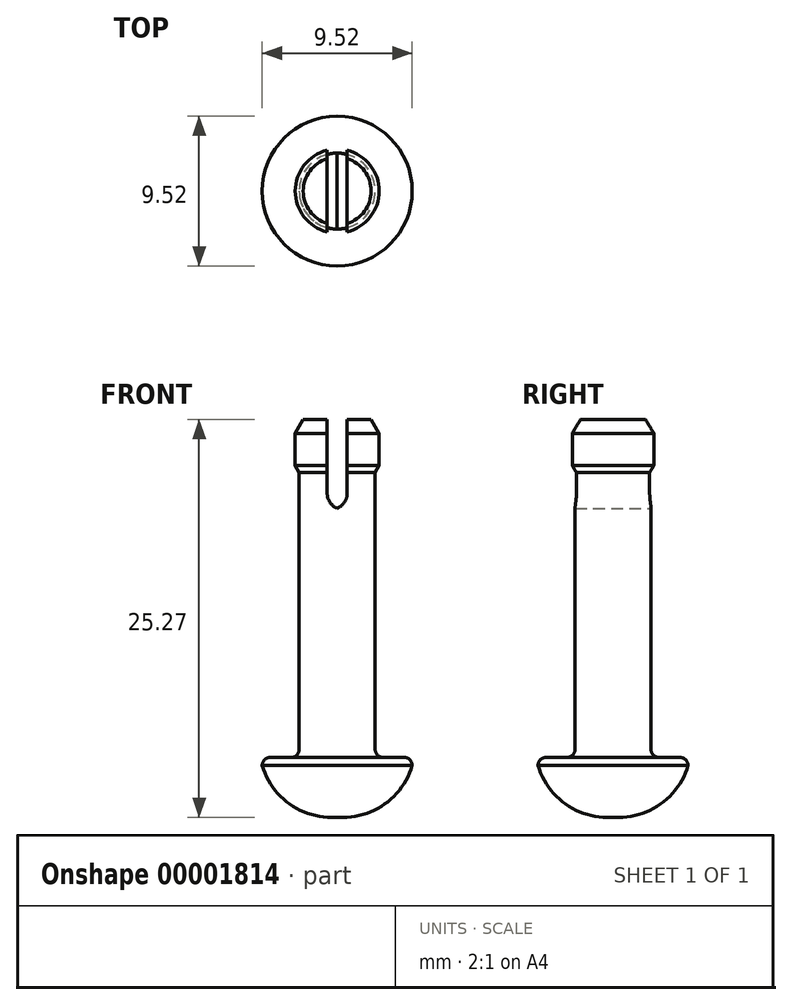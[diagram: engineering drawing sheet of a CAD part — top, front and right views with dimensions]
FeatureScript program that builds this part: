
annotation { "Feature Type Name" : "Feature", "Feature Type Description" : "" }
export const myFeature = defineFeature(function(context is Context, id is Id, definition is map)
    precondition{}
    {
        {
            var Q0;
            Q0=qCreatedBy(makeId("Front.planeOp"),FACE);
            var sketch = newSketch(context, id + "F0", { "sketchPlane" : qUnion([Q0])});
            skLineSegment(sketch, "E0", {"start": v(0, 0) * mm, "end": v(4.76, 0) * mm});
            skLineSegment(sketch, "E1", {"start": v(4.76, 0) * mm, "end": v(4.76, 3.8) * mm});
            skLineSegment(sketch, "E2", {"start": v(4.76, 3.81) * mm, "end": v(2.41, 3.81) * mm});
            skLineSegment(sketch, "E3", {"start": v(2.41, 3.81) * mm, "end": v(2.41, 21.46) * mm});
            skLineSegment(sketch, "E4", {"start": v(2.41, 21.46) * mm, "end": v(2.67, 21.46) * mm});
            skLineSegment(sketch, "E5", {"start": v(2.67, 21.46) * mm, "end": v(2.67, 25.27) * mm});
            skLineSegment(sketch, "E6", {"start": v(2.67, 25.27) * mm, "end": v(0, 25.27) * mm});
            skLineSegment(sketch, "E7", {"start": v(0, 25.27) * mm, "end": v(0, 0) * mm});
            skSolve(sketch);
        }
        {
            var Q0;
            Q0=makeQuery(id+"F0.imprint","IMPRINT",FACE,{"disambiguationData":[TD([[makeQuery(id+"F0.imprint","IMPRINT",EDGE,{"derivedFrom":sQuery(id+"F0.wireOp",EDGE,"E0")}),1.0]])]});
            var Q1;
            Q1=sQuery(id+"F0.wireOp",EDGE,"E7");
            revolve(context, id + "F1", {"entities" : qUnion([Q0]), "axis" : qUnion([Q1]), "revolveType" : RevolveType.FULL});
        }
        {
            var Q0;
            Q0=qCreatedBy(makeId("Front.planeOp"),FACE);
            var sketch = newSketch(context, id + "F2", { "sketchPlane" : qUnion([Q0])});
            skLineSegment(sketch, "E8.0", {"start": v(-2.67, 25.27) * mm, "end": v(2.67, 25.27) * mm});
            skLineSegment(sketch, "E9.rect.bottom", {"start": v(-0.63, 19.56) * mm, "end": v(0.64, 19.56) * mm});
            skLineSegment(sketch, "E9.rect.top", {"start": v(-0.63, 30.99) * mm, "end": v(0.64, 30.99) * mm});
            skLineSegment(sketch, "E9.rect.left", {"start": v(-0.63, 19.56) * mm, "end": v(-0.63, 30.99) * mm});
            skLineSegment(sketch, "E9.rect.right", {"start": v(0.64, 19.56) * mm, "end": v(0.64, 30.99) * mm});
            skPoint(sketch, "E9.rect.middle", {"position": v(0, 25.27) * mm});
            skSolve(sketch);
        }
        {
            var Q0;
            {var subQ3=sQuery(id+"F2.wireOp",EDGE,"E9.rect.bottom");Q0=makeQuery(id+"F2.imprint","IMPRINT",FACE,{"disambiguationData":[TD([[makeQuery(id+"F2.imprint","IMPRINT",EDGE,{"derivedFrom":subQ3}),1.0]])]});}
            extrude(context, id + "F3", {"entities" : qUnion([Q0]), "operationType" : NewBodyOperationType.REMOVE, "endBound" : BoundingType.SYMMETRIC, "oppositeDirection" : true, "depth" : 25.4 * mm});
        }
        {
            var Q0;
            Q0=makeQuery(id+"F3.boolean.opBoolean","COPY",EDGE,{"derivedFrom":makeQuery(id+"F3.opExtrude","SWEPT_EDGE",EDGE,{"disambiguationData":[OSD([sQuery(id+"F2.wireOp",EDGE,"E9.rect.bottom"),sQuery(id+"F2.wireOp",EDGE,"E9.rect.right")])]})});
            var Q1;
            Q1=makeQuery(id+"F3.boolean.opBoolean","COPY",EDGE,{"derivedFrom":makeQuery(id+"F3.opExtrude","SWEPT_EDGE",EDGE,{"disambiguationData":[OSD([sQuery(id+"F2.wireOp",EDGE,"E9.rect.bottom"),sQuery(id+"F2.wireOp",EDGE,"E9.rect.left")])]})});
            fillet(context, id + "F4", {"entities" : qUnion([Q0, Q1]), "radius" : 1.02 * mm, "tangentPropagation" : true, "allowEdgeOverflow" : false});
        }
        {
            var Q0;
            {var subQ0=sQuery(id+"F0.wireOp",EDGE,"E5");var subQ1=sQuery(id+"F0.wireOp",EDGE,"E6");Q0=makeQuery(id+"F3.boolean.opBoolean","SPLIT",EDGE,{"disambiguationData":[TD([makeQuery(id+"F3.opExtrude","SWEPT_FACE",FACE,{"disambiguationData":[OSD([sQuery(id+"F2.wireOp",EDGE,"E9.rect.right")])]})])],"derivedFrom":makeQuery(id+"F1.opRevolve","SWEPT_EDGE",EDGE,{"disambiguationData":[OSD([subQ0,subQ1])]})});}
            var Q1;
            {var subQ0=sQuery(id+"F0.wireOp",EDGE,"E4");var subQ1=sQuery(id+"F0.wireOp",EDGE,"E5");Q1=makeQuery(id+"F3.boolean.opBoolean","SPLIT",EDGE,{"disambiguationData":[TD([makeQuery(id+"F3.opExtrude","SWEPT_FACE",FACE,{"disambiguationData":[OSD([sQuery(id+"F2.wireOp",EDGE,"E9.rect.right")])]})])],"derivedFrom":makeQuery(id+"F1.opRevolve","SWEPT_EDGE",EDGE,{"disambiguationData":[OSD([subQ0,subQ1])]})});}
            var Q2;
            {var subQ0=sQuery(id+"F0.wireOp",EDGE,"E5");var subQ1=sQuery(id+"F0.wireOp",EDGE,"E6");Q2=makeQuery(id+"F3.boolean.opBoolean","SPLIT",EDGE,{"disambiguationData":[TD([makeQuery(id+"F3.opExtrude","SWEPT_FACE",FACE,{"disambiguationData":[OSD([sQuery(id+"F2.wireOp",EDGE,"E9.rect.left")])]})])],"derivedFrom":makeQuery(id+"F1.opRevolve","SWEPT_EDGE",EDGE,{"disambiguationData":[OSD([subQ0,subQ1])]})});}
            chamfer(context, id + "F5", {"entities" : qUnion([Q0, Q1, Q2]), "chamferType" : ChamferType.OFFSET_ANGLE, "width" : 0.5 * mm, "oppositeDirection" : false, "angle" : 60 * degree, "tangentPropagation" : true});
        }
        {
            var Q0;
            {var subQ0=sQuery(id+"F0.wireOp",EDGE,"E4");var subQ1=sQuery(id+"F0.wireOp",EDGE,"E5");Q0=makeQuery(id+"F3.boolean.opBoolean","SPLIT",EDGE,{"disambiguationData":[TD([makeQuery(id+"F3.opExtrude","SWEPT_FACE",FACE,{"disambiguationData":[OSD([sQuery(id+"F2.wireOp",EDGE,"E9.rect.left")])]})])],"derivedFrom":makeQuery(id+"F1.opRevolve","SWEPT_EDGE",EDGE,{"disambiguationData":[OSD([subQ0,subQ1])]})});}
            chamfer(context, id + "F6", {"entities" : qUnion([Q0]), "chamferType" : ChamferType.OFFSET_ANGLE, "width" : 0.89 * mm, "oppositeDirection" : false, "angle" : 30 * degree, "tangentPropagation" : true});
        }
        {
            var Q0;
            Q0=makeQuery(id+"F1.opRevolve","SWEPT_EDGE",EDGE,{"disambiguationData":[OSD([sQuery(id+"F0.wireOp",EDGE,"E2"),sQuery(id+"F0.wireOp",EDGE,"E3")])]});
            var Q1;
            Q1=makeQuery(id+"F1.opRevolve","SWEPT_EDGE",EDGE,{"disambiguationData":[OSD([sQuery(id+"F0.wireOp",EDGE,"E1"),sQuery(id+"F0.wireOp",EDGE,"E2")])]});
            fillet(context, id + "F7", {"entities" : qUnion([Q0, Q1]), "radius" : 0.5 * mm, "tangentPropagation" : true, "allowEdgeOverflow" : false});
        }
        {
            var Q0;
            Q0=makeQuery(id+"F1.opRevolve","SWEPT_EDGE",EDGE,{"disambiguationData":[OSD([sQuery(id+"F0.wireOp",EDGE,"E0"),sQuery(id+"F0.wireOp",EDGE,"E1")])]});
            fillet(context, id + "F8", {"entities" : qUnion([Q0]), "radius" : 4.57 * mm, "tangentPropagation" : true, "allowEdgeOverflow" : false});
        }
    });
